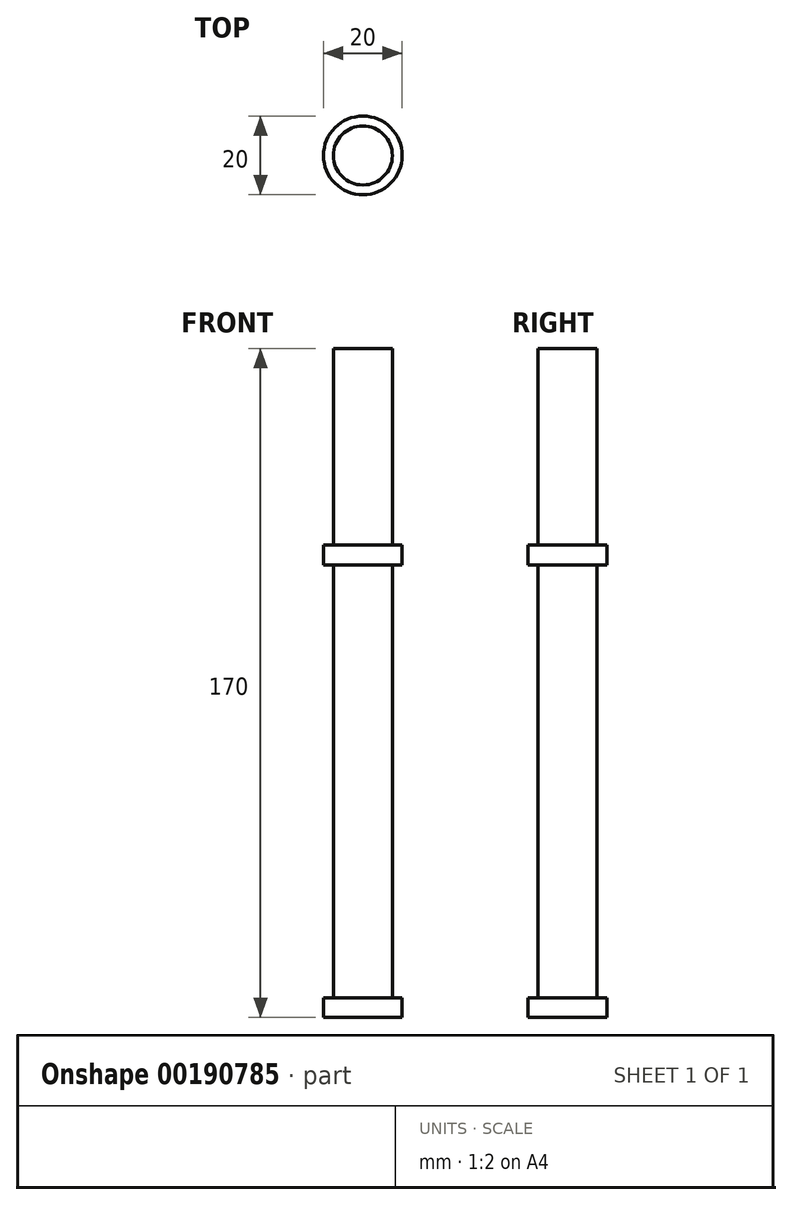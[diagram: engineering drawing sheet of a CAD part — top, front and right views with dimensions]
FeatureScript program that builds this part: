
annotation { "Feature Type Name" : "Feature", "Feature Type Description" : "" }
export const myFeature = defineFeature(function(context is Context, id is Id, definition is map)
    precondition{}
    {
        {
            var Q0;
            Q0=qCreatedBy(makeId("Front.planeOp"),FACE);
            var sketch = newSketch(context, id + "F0", { "sketchPlane" : qUnion([Q0])});
            skLineSegment(sketch, "E0", {"start": v(0, 60) * mm, "end": v(0, -60) * mm});
            skLineSegment(sketch, "E1", {"start": v(0, 60) * mm, "end": v(10, 60) * mm});
            skLineSegment(sketch, "E2", {"start": v(10, 60) * mm, "end": v(10, 55) * mm});
            skLineSegment(sketch, "E3", {"start": v(10, 55) * mm, "end": v(7.5, 55) * mm});
            skLineSegment(sketch, "E4", {"start": v(7.5, 55) * mm, "end": v(7.5, 0) * mm});
            skLineSegment(sketch, "E5.MirrorCS", {"start": v(7.5, -55) * mm, "end": v(7.5, 0) * mm});
            skLineSegment(sketch, "E6.MirrorCS", {"start": v(10, -55) * mm, "end": v(7.5, -55) * mm});
            skLineSegment(sketch, "E7.MirrorCS", {"start": v(10, -60) * mm, "end": v(10, -55) * mm});
            skLineSegment(sketch, "E8.MirrorCS", {"start": v(0, -60) * mm, "end": v(10, -60) * mm});
            skSolve(sketch);
        }
        {
            var Q0;
            Q0=makeQuery(id+"F0.imprint","IMPRINT",FACE,{"disambiguationData":[TD([[makeQuery(id+"F0.imprint","IMPRINT",EDGE,{"derivedFrom":sQuery(id+"F0.wireOp",EDGE,"E0")}),1.0]])]});
            var Q1;
            Q1=sQuery(id+"F0.wireOp",EDGE,"E0");
            revolve(context, id + "F1", {"entities" : qUnion([Q0]), "axis" : qUnion([Q1]), "revolveType" : RevolveType.FULL});
        }
        {
            var Q0;
            Q0=makeQuery(id+"F1.opRevolve","SWEPT_FACE",FACE,{"disambiguationData":[OSD([sQuery(id+"F0.wireOp",EDGE,"E1")])]});
            var sketch = newSketch(context, id + "F2", { "sketchPlane" : qUnion([Q0])});
            skCircle(sketch, "E9", {"center": v(0, 0) * mm, "radius": 7.5 * mm});
            skSolve(sketch);
        }
        {
            var Q0;
            Q0=makeQuery(id+"F2.imprint","IMPRINT",FACE,{"disambiguationData":[TD([[makeQuery(id+"F2.imprint","IMPRINT",EDGE,{"derivedFrom":sQuery(id+"F2.wireOp",EDGE,"E9")}),1.0]])]});
            extrude(context, id + "F3", {"entities" : qUnion([Q0]), "operationType" : NewBodyOperationType.ADD, "depth" : 50 * mm});
        }
    });
